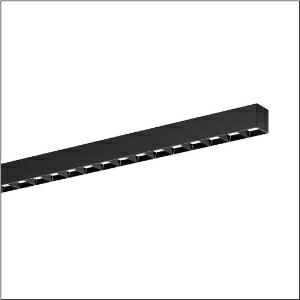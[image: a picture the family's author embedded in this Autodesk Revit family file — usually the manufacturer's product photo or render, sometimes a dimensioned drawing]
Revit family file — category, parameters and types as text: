
# Revit family: silica_r__21_51mx21tctab_539a
name_source: partatom
category: Lighting Fixtures
units: mm (PartAtom-declared; Revit-internal decimal feet)

## family parameters
Cut with Voids When Loaded = No
Host = Face
Light Source = No
Part Type = Normal
Room Calculation Point = No
Round Connector Dimension = Use Diameter
Shared = No

## types (1)
- --- (1 x LED, 9300 lm, 80.5 W, 6500K)
    Apparent Load = 81 VA
    CIE Flux Codes = 85 99 100 100 100
    Color Rendering = 80
    Color Temperature = 6500K
    Default Elevation = 1800 mm
    Description = Silica® 21, office luminaire, primary light control with darklight reflector, of PMMA, black, CAT 2 (L<= 3000cd/m²), light emission: direct distribution, primary light characteristic: symmetric, installation type: surface-mounted, LED, rated luminous flux: 9.300lm, luminous efficacy: 110lm/W, light colour: 8tw, colour temperature: 2700..6500K, control gear: ECG DALI, with terminal, 3+2-pole, max. 2.5mm², mains connection: 220..240V, AC, 50/60Hz, rated input power: 84.6W, luminaire housing, of aluminium, jet black (RAL 9005), length: 3.004mm, width: 53mm, height: 53mm, protection rating (complete): IP20, insulation class (complete): insulation class I (protective earthing), certification: CE, permissible operating ambient temperature: 0..+35°C, standard: EN 50419, packaging unit: 1 piece
    Height = 0 mm  [stored 0 ft]
    Lamp = 1 x LED
    Lamp Light Flux = 9300 lm
    Lamp Power = 80.5 W
    Lamp count = 1
    Length = 3004 mm
    Luminous efficacy = 116 lm/W
    Manufacturer = Siteco
    ModVariant = No
    Model = 51MX21TCTAB
    Mounting Place = Ceiling
    Mounting Type = Recessed
    Number of Poles = 1
    OnlyDefault = Yes
    Power Factor = 1
    Product Name = Silica® 21
    Product group = office luminaire | ceiling recessed
    ProductGroupID = 400
    Protection Class = Protection class I
    Protection Degree = IP 20
    RLX_Detail_Level = 1
    RLX_Emergency_Light_Flux = 0 lm
    RLX_Emergency_Type = 0
    RLX_Emergency_Type_DB = No
    RlxData = <blob elided: 60933 chars, md5=6aecc6cb>
    Socket = socket
    Standby Power = 0 W
    System Light Flux = 9300 lm
    System Power = 81 W
    Type Comments = individual setting
    Type Image = l_1335908.jpg
    URL = http://relux.com
    VarID = @adj_109861
    Voltage = 0 V
    Weight = 0.00 kg
    Width = 53 mm

note: [stored X ft] marks values corroborated as IEEE doubles in the binary element streams (Revit-internal decimal feet)

## geometry (parser evidence)
native form markers: Blend x4, Sweep x11
no freeform markers — native parametric forms only
